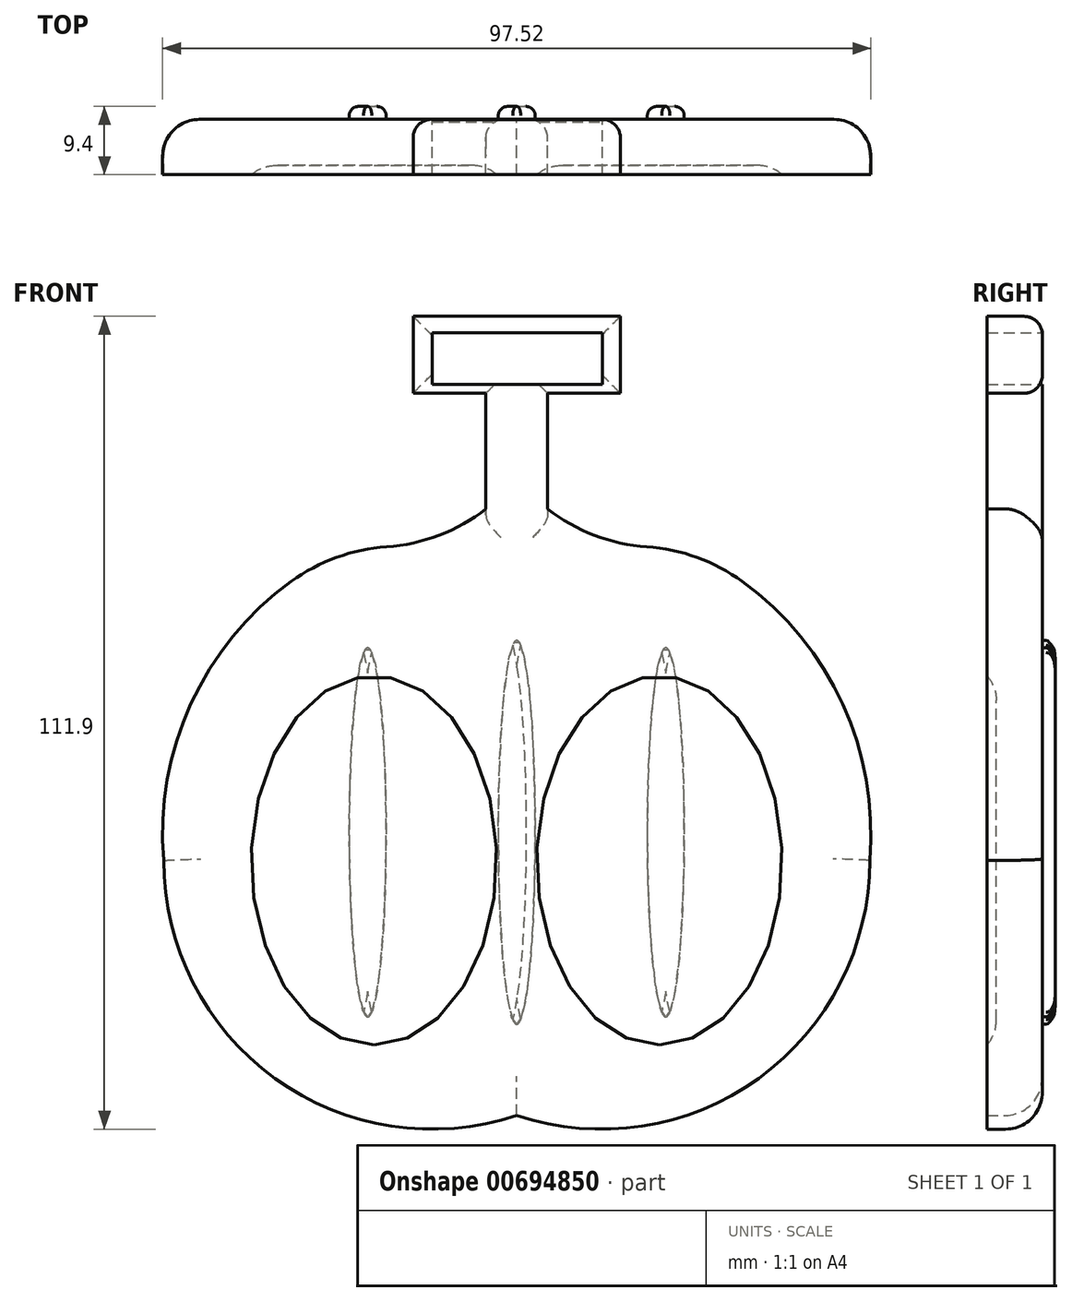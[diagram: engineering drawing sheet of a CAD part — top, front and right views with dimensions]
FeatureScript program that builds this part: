
annotation { "Feature Type Name" : "Feature", "Feature Type Description" : "" }
export const myFeature = defineFeature(function(context is Context, id is Id, definition is map)
    precondition{}
    {
        {
            var Q0;
            Q0=qCreatedBy(makeId("Front.planeOp"),FACE);
            var sketch = newSketch(context, id + "F0", { "sketchPlane" : qUnion([Q0])});
            skLineSegment(sketch, "E0", {"start": v(0, 56) * mm, "end": v(0, -59.32) * mm, "construction": true});
            skPoint(sketch, "E1.end.orphan", {"position": v(-48.6, -19.03) * mm});
            skPoint(sketch, "E2.start.orphan", {"position": v(-48.6, -22) * mm});
            skLineSegment(sketch, "E3", {"start": v(0, 55.86) * mm, "end": v(-14.27, 55.86) * mm});
            skLineSegment(sketch, "E4", {"start": v(-14.27, 55.86) * mm, "end": v(-14.27, 45.27) * mm});
            skLineSegment(sketch, "E5", {"start": v(-14.27, 45.27) * mm, "end": v(-4.25, 45.27) * mm});
            skLineSegment(sketch, "E6", {"start": v(-4.25, 45.27) * mm, "end": v(-4.25, 29.35) * mm});
            skArc(sketch, "E7", {"start": v(-17.9, 24.13) * mm, "mid": v(-10.68, 25.73) * mm, "end": v(-4.25, 29.35) * mm});
            skArc(sketch, "E8", {"start": v(-31.06, 19.36) * mm, "mid": v(-44.88, 2.47) * mm, "end": v(-48.6, -19.03) * mm});
            skArc(sketch, "E9", {"start": v(-48.6, -19.03) * mm, "mid": v(-33.3, -49.05) * mm, "end": v(0, -54.15) * mm});
            skArc(sketch, "E10.MirrorCS", {"start": v(17.9, 24.13) * mm, "mid": v(10.68, 25.73) * mm, "end": v(4.25, 29.35) * mm});
            skLineSegment(sketch, "E11.MirrorCS", {"start": v(4.25, 45.27) * mm, "end": v(4.25, 29.35) * mm});
            skLineSegment(sketch, "E12.MirrorCS", {"start": v(0, 55.86) * mm, "end": v(14.27, 55.86) * mm});
            skArc(sketch, "E13.MirrorCS", {"start": v(31.06, 19.36) * mm, "mid": v(44.88, 2.47) * mm, "end": v(48.6, -19.03) * mm});
            skArc(sketch, "E14.MirrorCS", {"start": v(48.6, -19.03) * mm, "mid": v(33.3, -49.05) * mm, "end": v(0, -54.15) * mm});
            skLineSegment(sketch, "E15.MirrorCS", {"start": v(14.27, 45.27) * mm, "end": v(4.25, 45.27) * mm});
            skLineSegment(sketch, "E16.MirrorCS", {"start": v(14.27, 55.86) * mm, "end": v(14.27, 45.27) * mm});
            skLineSegment(sketch, "E17", {"start": v(-7.13, 46.47) * mm, "end": v(0, 46.47) * mm});
            skLineSegment(sketch, "E18.MirrorCS", {"start": v(7.13, 46.47) * mm, "end": v(0, 46.47) * mm});
            skPoint(sketch, "E19.visualSharp", {"position": v(22.38, 24.22) * mm});
            skArc(sketch, "E19.filletArc", {"start": v(31.06, 19.36) * mm, "mid": v(24.81, 22.67) * mm, "end": v(17.9, 24.13) * mm});
            skPoint(sketch, "E20.visualSharp", {"position": v(-22.38, 24.22) * mm});
            skArc(sketch, "E20.filletArc", {"start": v(-17.9, 24.13) * mm, "mid": v(-24.81, 22.67) * mm, "end": v(-31.06, 19.36) * mm});
            skPoint(sketch, "E21", {"position": v(-7.13, 55.86) * mm});
            skPoint(sketch, "E22", {"position": v(-14.27, 50.56) * mm});
            skPoint(sketch, "E23.end.orphan", {"position": v(0, 50.56) * mm});
            skPoint(sketch, "E24.MirrorCS.start.orphan", {"position": v(7.13, 50.56) * mm});
            skPoint(sketch, "E25.start.orphan", {"position": v(-7.13, 50.56) * mm});
            skPoint(sketch, "E26.MirrorCS.end.orphan", {"position": v(7.13, 46.47) * mm});
            skLineSegment(sketch, "E27", {"start": v(-11.62, 53.61) * mm, "end": v(-11.62, 46.47) * mm});
            skLineSegment(sketch, "E28", {"start": v(-11.62, 46.47) * mm, "end": v(-7.13, 46.47) * mm});
            skLineSegment(sketch, "E29", {"start": v(11.8, 46.47) * mm, "end": v(7.13, 46.47) * mm});
            skLineSegment(sketch, "E30", {"start": v(11.8, 46.47) * mm, "end": v(11.8, 53.61) * mm});
            skLineSegment(sketch, "E31", {"start": v(11.8, 53.61) * mm, "end": v(-11.62, 53.61) * mm});
            skSolve(sketch);
        }
        {
            var Q0;
            Q0 = qSketchRegion(id + "F0", true);
            extrude(context, id + "F1", {"entities" : qUnion([Q0]), "depth" : 7.62 * mm, "offsetDistance" : 25.4 * mm});
        }
        {
            var Q0;
            Q0=makeQuery(id+"F1.opExtrude","CAP_EDGE",EDGE,{"disambiguationData":[OSD([sQuery(id+"F0.wireOp",EDGE,"E8")])],"isStart":true});
            var Q1;
            Q1=makeQuery(id+"F1.opExtrude","CAP_EDGE",EDGE,{"disambiguationData":[OSD([sQuery(id+"F0.wireOp",EDGE,"E9")])],"isStart":true});
            var Q2;
            Q2=makeQuery(id+"F1.opExtrude","CAP_EDGE",EDGE,{"disambiguationData":[OSD([sQuery(id+"F0.wireOp",EDGE,"E14.MirrorCS")])],"isStart":true});
            var Q3;
            Q3=makeQuery(id+"F1.opExtrude","CAP_EDGE",EDGE,{"disambiguationData":[OSD([sQuery(id+"F0.wireOp",EDGE,"E13.MirrorCS")])],"isStart":true});
            fillet(context, id + "F2", {"entities" : qUnion([Q0, Q1, Q2, Q3]), "radius" : 5.08 * mm, "tangentPropagation" : true, "allowEdgeOverflow" : false});
        }
        {
            var Q0;
            Q0=makeQuery(id+"F1.opExtrude","CAP_EDGE",EDGE,{"disambiguationData":[OSD([sQuery(id+"F0.wireOp",EDGE,"E11.MirrorCS")])],"isStart":true});
            var Q1;
            Q1=makeQuery(id+"F1.opExtrude","CAP_EDGE",EDGE,{"disambiguationData":[OSD([sQuery(id+"F0.wireOp",EDGE,"E6")])],"isStart":true});
            var Q2;
            Q2=makeQuery(id+"F1.opExtrude","CAP_EDGE",EDGE,{"disambiguationData":[OSD([sQuery(id+"F0.wireOp",EDGE,"E5")])],"isStart":true});
            var Q3;
            Q3=makeQuery(id+"F1.opExtrude","CAP_EDGE",EDGE,{"disambiguationData":[OSD([sQuery(id+"F0.wireOp",EDGE,"E15.MirrorCS")])],"isStart":true});
            var Q4;
            Q4=makeQuery(id+"F1.opExtrude","CAP_EDGE",EDGE,{"disambiguationData":[OSD([sQuery(id+"F0.wireOp",EDGE,"E3"),sQuery(id+"F0.wireOp",EDGE,"E12.MirrorCS")])],"isStart":true});
            var Q5;
            Q5=makeQuery(id+"F1.opExtrude","CAP_EDGE",EDGE,{"disambiguationData":[OSD([sQuery(id+"F0.wireOp",EDGE,"E4")])],"isStart":true});
            var Q6;
            Q6=makeQuery(id+"F1.opExtrude","CAP_EDGE",EDGE,{"disambiguationData":[OSD([sQuery(id+"F0.wireOp",EDGE,"E16.MirrorCS")])],"isStart":true});
            fillet(context, id + "F3", {"entities" : qUnion([Q0, Q1, Q2, Q3, Q4, Q5, Q6]), "radius" : 2.54 * mm, "tangentPropagation" : true, "allowEdgeOverflow" : false});
        }
        {
            var Q0;
            Q0=makeQuery(id+"F1.opExtrude","CAP_FACE",FACE,{"disambiguationData":[OSD([sQuery(id+"F0.wireOp",EDGE,"E3"),sQuery(id+"F0.wireOp",EDGE,"E4"),sQuery(id+"F0.wireOp",EDGE,"E5"),sQuery(id+"F0.wireOp",EDGE,"E6"),sQuery(id+"F0.wireOp",EDGE,"E7"),sQuery(id+"F0.wireOp",EDGE,"E8"),sQuery(id+"F0.wireOp",EDGE,"E9"),sQuery(id+"F0.wireOp",EDGE,"E10.MirrorCS"),sQuery(id+"F0.wireOp",EDGE,"E11.MirrorCS"),sQuery(id+"F0.wireOp",EDGE,"E12.MirrorCS"),sQuery(id+"F0.wireOp",EDGE,"E13.MirrorCS"),sQuery(id+"F0.wireOp",EDGE,"E14.MirrorCS"),sQuery(id+"F0.wireOp",EDGE,"E15.MirrorCS"),sQuery(id+"F0.wireOp",EDGE,"E16.MirrorCS"),sQuery(id+"F0.wireOp",EDGE,"E25"),sQuery(id+"F0.wireOp",EDGE,"E17"),sQuery(id+"F0.wireOp",EDGE,"E23"),sQuery(id+"F0.wireOp",EDGE,"E24.MirrorCS"),sQuery(id+"F0.wireOp",EDGE,"E18.MirrorCS"),sQuery(id+"F0.wireOp",EDGE,"E26.MirrorCS"),sQuery(id+"F0.wireOp",EDGE,"E19.filletArc"),sQuery(id+"F0.wireOp",EDGE,"E20.filletArc")])],"isStart":false});
            var sketch = newSketch(context, id + "F4", { "sketchPlane" : qUnion([Q0])});
            skEllipse(sketch, "E32", {"center": v(-19.65, -19.03) * mm, "majorRadius": 25.4 * mm, "minorRadius": 16.9 * mm, "majorAxis": v(0, -1)});
            skEllipse(sketch, "E33", {"center": v(19.65, -19.03) * mm, "majorRadius": 25.4 * mm, "minorRadius": 16.9 * mm, "majorAxis": v(0, -1)});
            skSolve(sketch);
        }
        {
            var Q0;
            Q0 = qSketchRegion(id + "F4", true);
            extrude(context, id + "F5", {"entities" : qUnion([Q0]), "operationType" : NewBodyOperationType.REMOVE, "oppositeDirection" : true, "depth" : 1.27 * mm, "offsetDistance" : 25.4 * mm});
        }
        {
            var Q0;
            Q0=makeQuery(id+"F5.boolean.opBoolean","COPY",EDGE,{"derivedFrom":makeQuery(id+"F5.opExtrude","CAP_EDGE",EDGE,{"disambiguationData":[OSD([sQuery(id+"F4.wireOp",EDGE,"E32")])],"isStart":false})});
            var Q1;
            Q1=makeQuery(id+"F5.boolean.opBoolean","COPY",EDGE,{"derivedFrom":makeQuery(id+"F5.opExtrude","CAP_EDGE",EDGE,{"disambiguationData":[OSD([sQuery(id+"F4.wireOp",EDGE,"E33")])],"isStart":false})});
            fillet(context, id + "F6", {"entities" : qUnion([Q0, Q1]), "radius" : 5.08 * mm, "tangentPropagation" : true, "allowEdgeOverflow" : false});
        }
        {
            var Q0;
            Q0=makeQuery(id+"F1.opExtrude","CAP_FACE",FACE,{"disambiguationData":[OSD([sQuery(id+"F0.wireOp",EDGE,"E3"),sQuery(id+"F0.wireOp",EDGE,"E4"),sQuery(id+"F0.wireOp",EDGE,"E5"),sQuery(id+"F0.wireOp",EDGE,"E6"),sQuery(id+"F0.wireOp",EDGE,"E7"),sQuery(id+"F0.wireOp",EDGE,"E8"),sQuery(id+"F0.wireOp",EDGE,"E9"),sQuery(id+"F0.wireOp",EDGE,"E10.MirrorCS"),sQuery(id+"F0.wireOp",EDGE,"E11.MirrorCS"),sQuery(id+"F0.wireOp",EDGE,"E12.MirrorCS"),sQuery(id+"F0.wireOp",EDGE,"E13.MirrorCS"),sQuery(id+"F0.wireOp",EDGE,"E14.MirrorCS"),sQuery(id+"F0.wireOp",EDGE,"E15.MirrorCS"),sQuery(id+"F0.wireOp",EDGE,"E16.MirrorCS"),sQuery(id+"F0.wireOp",EDGE,"E25"),sQuery(id+"F0.wireOp",EDGE,"E17"),sQuery(id+"F0.wireOp",EDGE,"E23"),sQuery(id+"F0.wireOp",EDGE,"E24.MirrorCS"),sQuery(id+"F0.wireOp",EDGE,"E18.MirrorCS"),sQuery(id+"F0.wireOp",EDGE,"E26.MirrorCS"),sQuery(id+"F0.wireOp",EDGE,"E19.filletArc"),sQuery(id+"F0.wireOp",EDGE,"E20.filletArc")])],"isStart":true});
            var sketch = newSketch(context, id + "F7", { "sketchPlane" : qUnion([Q0])});
            skEllipse(sketch, "E34", {"center": v(0, -15.18) * mm, "majorRadius": 26.42 * mm, "minorRadius": 2.54 * mm, "majorAxis": v(0, -1)});
            skEllipse(sketch, "E35", {"center": v(20.52, -15.18) * mm, "majorRadius": 25.4 * mm, "minorRadius": 2.54 * mm, "majorAxis": v(0, -1)});
            skEllipse(sketch, "E36", {"center": v(-20.52, -15.18) * mm, "majorRadius": 25.4 * mm, "minorRadius": 2.54 * mm, "majorAxis": v(0, -1)});
            skSolve(sketch);
        }
        {
            var Q0;
            Q0 = qSketchRegion(id + "F7", true);
            extrude(context, id + "F8", {"entities" : qUnion([Q0]), "operationType" : NewBodyOperationType.ADD, "depth" : 1.78 * mm, "offsetDistance" : 25.4 * mm});
        }
        {
            var Q0;
            Q0=makeQuery(id+"F8.opExtrude","CAP_EDGE",EDGE,{"disambiguationData":[OSD([sQuery(id+"F7.wireOp",EDGE,"E36")])],"isStart":false});
            var Q1;
            Q1=makeQuery(id+"F8.opExtrude","CAP_EDGE",EDGE,{"disambiguationData":[OSD([sQuery(id+"F7.wireOp",EDGE,"E34")])],"isStart":false});
            var Q2;
            Q2=makeQuery(id+"F8.opExtrude","CAP_EDGE",EDGE,{"disambiguationData":[OSD([sQuery(id+"F7.wireOp",EDGE,"E35")])],"isStart":false});
            fillet(context, id + "F9", {"entities" : qUnion([Q0, Q1, Q2]), "radius" : 1.27 * mm, "tangentPropagation" : true, "allowEdgeOverflow" : false});
        }
    });
